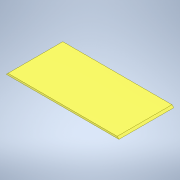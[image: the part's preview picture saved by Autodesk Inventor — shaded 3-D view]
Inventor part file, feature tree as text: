
AUTODESK INVENTOR PART (.ipt)
format: ipt  version: 2021.2 (Build 252289000, 289)  size: 109,568 bytes
history: native  units: in
note: dims shown in document units (in); Inventor stores cm internally (conversion verified against a paired STEP export)
features: extrude x2, sketch x2
ambient origin geometry x8: Origin, YZ Plane, XZ Plane, XY Plane, X Axis, Y Axis, Z Axis, Center Point
bodies: Solid1 (feature_tree)
feature tree (4):
  extrude  "Extrusion1"  Depth=3.8861in
  extrude  "Extrusion2"  TaperAngle=0.0deg  [1 undecoded]
  sketch  "Sketch2"  dims[d0=3.8861in d1=8.0in]
  sketch  "Sketch3"  dims[d2=0.125in d3=0.0in d4=45.0deg d5=45.0deg d6=0.0in d7=0.0in]
note: 1 required parameter value undecoded (feature->parameter linkage not recoverable at this tier; creation-order binding heuristic only, values carry confidence <= 0.55)
